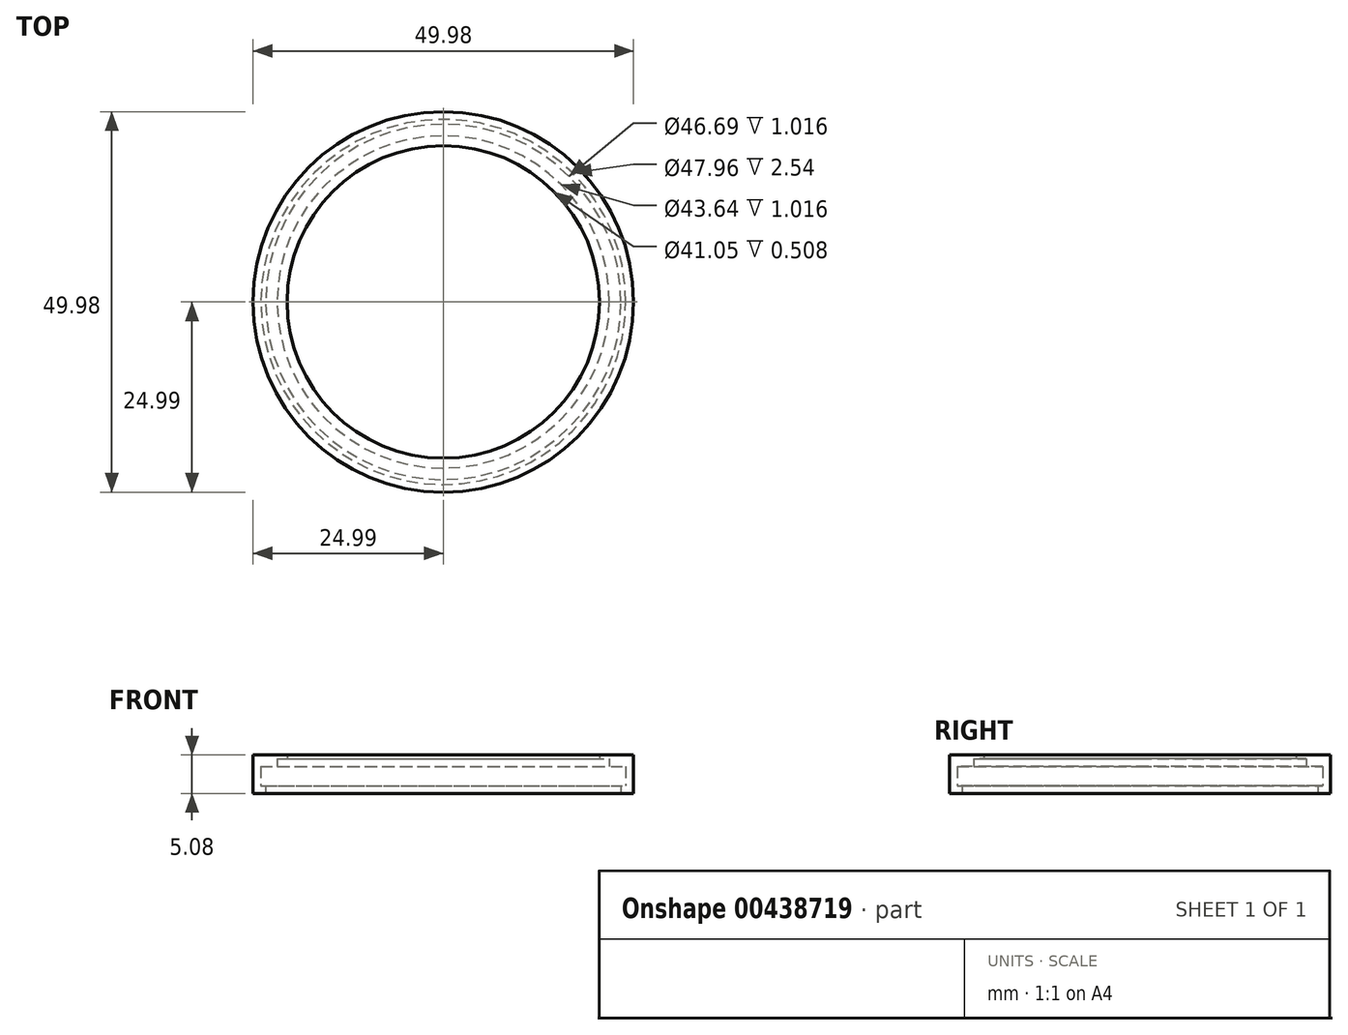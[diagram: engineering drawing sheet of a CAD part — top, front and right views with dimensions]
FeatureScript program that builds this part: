
annotation { "Feature Type Name" : "Feature", "Feature Type Description" : "" }
export const myFeature = defineFeature(function(context is Context, id is Id, definition is map)
    precondition{}
    {
        {
            var Q0;
            Q0=qCreatedBy(makeId("Front.planeOp"),FACE);
            var sketch = newSketch(context, id + "F0", { "sketchPlane" : qUnion([Q0])});
            skLineSegment(sketch, "E0", {"start": v(0, 0) * mm, "end": v(-25, 0) * mm});
            skLineSegment(sketch, "E1", {"start": v(-25, 0) * mm, "end": v(-25, 5.08) * mm});
            skLineSegment(sketch, "E2", {"start": v(-25, 5.08) * mm, "end": v(-20.52, 5.08) * mm});
            skLineSegment(sketch, "E3", {"start": v(-20.52, 5.08) * mm, "end": v(-20.52, 4.57) * mm});
            skLineSegment(sketch, "E4", {"start": v(-20.52, 4.57) * mm, "end": v(-21.82, 4.57) * mm});
            skLineSegment(sketch, "E5", {"start": v(-21.82, 4.57) * mm, "end": v(-21.82, 3.56) * mm});
            skLineSegment(sketch, "E6", {"start": v(-21.82, 3.56) * mm, "end": v(-23.98, 3.56) * mm});
            skLineSegment(sketch, "E7", {"start": v(-23.98, 3.56) * mm, "end": v(-23.98, 1.02) * mm});
            skLineSegment(sketch, "E8", {"start": v(-23.98, 1.02) * mm, "end": v(-23.34, 1.02) * mm});
            skLineSegment(sketch, "E9", {"start": v(-23.34, 1.02) * mm, "end": v(-23.34, 0) * mm});
            skLineSegment(sketch, "E10", {"start": v(-23.34, 0) * mm, "end": v(-25, 0) * mm});
            skSolve(sketch);
        }
        {
            var Q0;
            Q0=qCreatedBy(makeId("Front.planeOp"),FACE);
            var sketch = newSketch(context, id + "F1", { "sketchPlane" : qUnion([Q0])});
            skLineSegment(sketch, "E11", {"start": v(0, 0) * mm, "end": v(0, 11.21) * mm});
            skSolve(sketch);
        }
        {
            var Q0;
            Q0=makeQuery(id+"F0.imprint","IMPRINT",FACE,{"disambiguationData":[TD([[makeQuery(id+"F0.imprint","IMPRINT",EDGE,{"derivedFrom":sQuery(id+"F0.wireOp",EDGE,"E1")}),-1.0]])]});
            var Q1;
            Q1=sQuery(id+"F1.wireOp",EDGE,"E11");
            revolve(context, id + "F2", {"entities" : qUnion([Q0]), "axis" : qUnion([Q1]), "revolveType" : RevolveType.FULL});
        }
    });
